# Revit family: Gira_123928
name_source: partatom
category: Electrical Fixtures
revit_build: Autodesk Revit 2017 (Build: 20160225_1515(x64)
units: mm (PartAtom-declared; Revit-internal decimal feet)

## family parameters
Cut with Voids When Loaded = No
Host = Face
Maintain Annotation Orientation = No
Part Type = Normal
Room Calculation Point = No
Round Connector Dimension = Use Diameter
Shared = No

## types (1)
- Wohnungsstation Video AP Plus System 55 Anthrazit
    Abhörsicher = Yes
    Available = Yes
    Bedienung Türöffner = Yes
    Bildsystem = PAL
    Category = Innenstation für Türkommunikation
    Data sheet (1) = https://katalog.gira.de
    Default Elevation = 1219 mm
    Farbe = weiß
    Funktions-Lampen = Yes
    GTIN = 4010337016229
    HAN = 123901
    HeinzeBIM = https://bimportal.heinze.de
    Hörgerätekompatibel = No
    Installationstechnik = Bus-System
    Internkommunikation = Yes
    Keynote = Sys55_Wohnungsstation_Abdeckung
    Lautstärkeregelung = Yes
    Manufacturer URL = https://www.gira.de
    Mit Memory-Funktion = No
    Mit Touchscreen = No
    Mit Türöffnerautomatik = Yes
    Mit Video = Yes
    Montageart = auf Putz
    Name = Wohnungsstation Video AP Plus System 55 Cremeweiß
    Region = DE
    Rufabschaltung = Yes
    Rufunterscheidung = Yes
    Schaltfunktionen = Yes
    URL = http://katalog.gira.de
    Verbindung mit Smartphone möglich = No
    Werkstoff = sonstige
    Zusatzgerät anreihbar = No

## geometry (parser evidence)
native form markers: Blend x2, Sweep x3
no freeform markers — native parametric forms only
